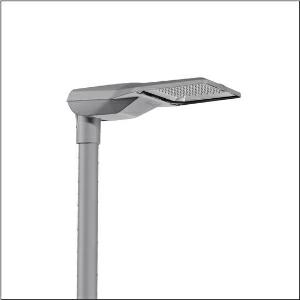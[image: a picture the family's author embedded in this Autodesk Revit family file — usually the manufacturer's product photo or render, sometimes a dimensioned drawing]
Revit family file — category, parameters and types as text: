
# Revit family: streetlight_sl_21_midi___pc-l_5xe7f33a08mb_bf39
name_source: partatom
category: Lighting Fixtures
units: mm (PartAtom-declared; Revit-internal decimal feet)

## family parameters
Cut with Voids When Loaded = No
Host = Face
Light Source = No
Part Type = Normal
Room Calculation Point = No
Round Connector Dimension = Use Diameter
Shared = No

## types (1)
- --- (1 x LED, 17390 lm, 136 W, 3000K)
    Apparent Load = 136 VA
    CIE Flux Codes = 38 78 98 100 100
    Color Rendering = 70
    Color Temperature = 3000K
    Default Elevation = 1800 mm
    Description = Streetlight SL 21 midi, mast luminaire, primary light control with lens, of PMMA, primary optical cover: cover, of toughened safety glass, transparent, light distribution: PC-L, light emission: direct distribution, primary light characteristic: asymmetric, left, installation type: post-top, side-entry, LED, 3G 1.5mm², High Power LED, rated luminous flux: 17.390lm, luminous efficacy: 128lm/W, light colour: 730, colour temperature: 3000K, control: overheat protection, constant luminous flux control, time-dependent luminous flux control, flexible luminous flux parameterisation, mains connection: 220..240V, AC, 50/60Hz, connection cable pre-assembled, cable length: 12,5m, wiring characteristics: H07RN-F, start of lifetime: 136W, end of service life: 142W, reduction: 61W, luminaire housing, of diecast aluminium, powder-coated, Siteco® metallic grey (DB 702S), corrosivity category C5 mid according to DIN EN ISO 12944, please order mast flange separately, inclination adjustable: 0°, 5°, 10°, 15°, sealing non-destructively replaceable, multi-level sealing system, length: 644mm, width: 335mm, height: 110mm, mast flange for spigot size: 42mm (side-entry): 5XC10008XM4, 60/48mm (side-entry/post-top): 5XC10108XM2, 76/60mm (side-entry/post-top): 5XC10108XM1, protection rating (complete): IP66, insulation class (complete): insulation class II (safety insulation), certification: CE, ENEC, ENEC+, VDE, impact resistance: IK09, permissible operating ambient temperature for outdoor applications: -40..+50°C, standard-compliant lighting for roads and squares, packaging unit: 1 piece

Light Distribution: PC-L
    Height = 111 mm
    Lamp = 1 x LED
    Lamp Light Flux = 17390 lm
    Lamp Power = 136 W
    Lamp count = 1
    Length = 644 mm
    Luminous efficacy = 128 lm/W
    Manufacturer = Siteco
    ModVariant = No
    Model = 5XE7F33A08MB
    Number of Poles = 1
    OnlyDefault = Yes
    Power Factor = 1
    Product Name = Streetlight SL 21 midi | PC-L
    Product group = mast luminaire | pylon top
    ProductGroupID = 6100
    Protection Class = Protection class II
    Protection Degree = IP 66
    RLX_Detail_Level = 1
    RLX_Emergency_Light_Flux = 0 lm
    RLX_Emergency_Type = 0
    RLX_Emergency_Type_DB = No
    RlxData = <blob elided: 92833 chars, md5=8a40bdf2>
    Socket = socket
    Standby Power = 0 W
    System Light Flux = 17390 lm
    System Power = 136 W
    Type Comments = factory setting: luminous flux: 100 % | Output Level: 100 % | 695 mA
    Type Image = l_1004298.jpg
    URL = http://relux.com
    VarID = @adj_023179
    Voltage = 0 V
    Weight = 0.00 kg
    Width = 336 mm

## geometry (parser evidence)
native form markers: Blend x4, Sweep x9
no freeform markers — native parametric forms only
